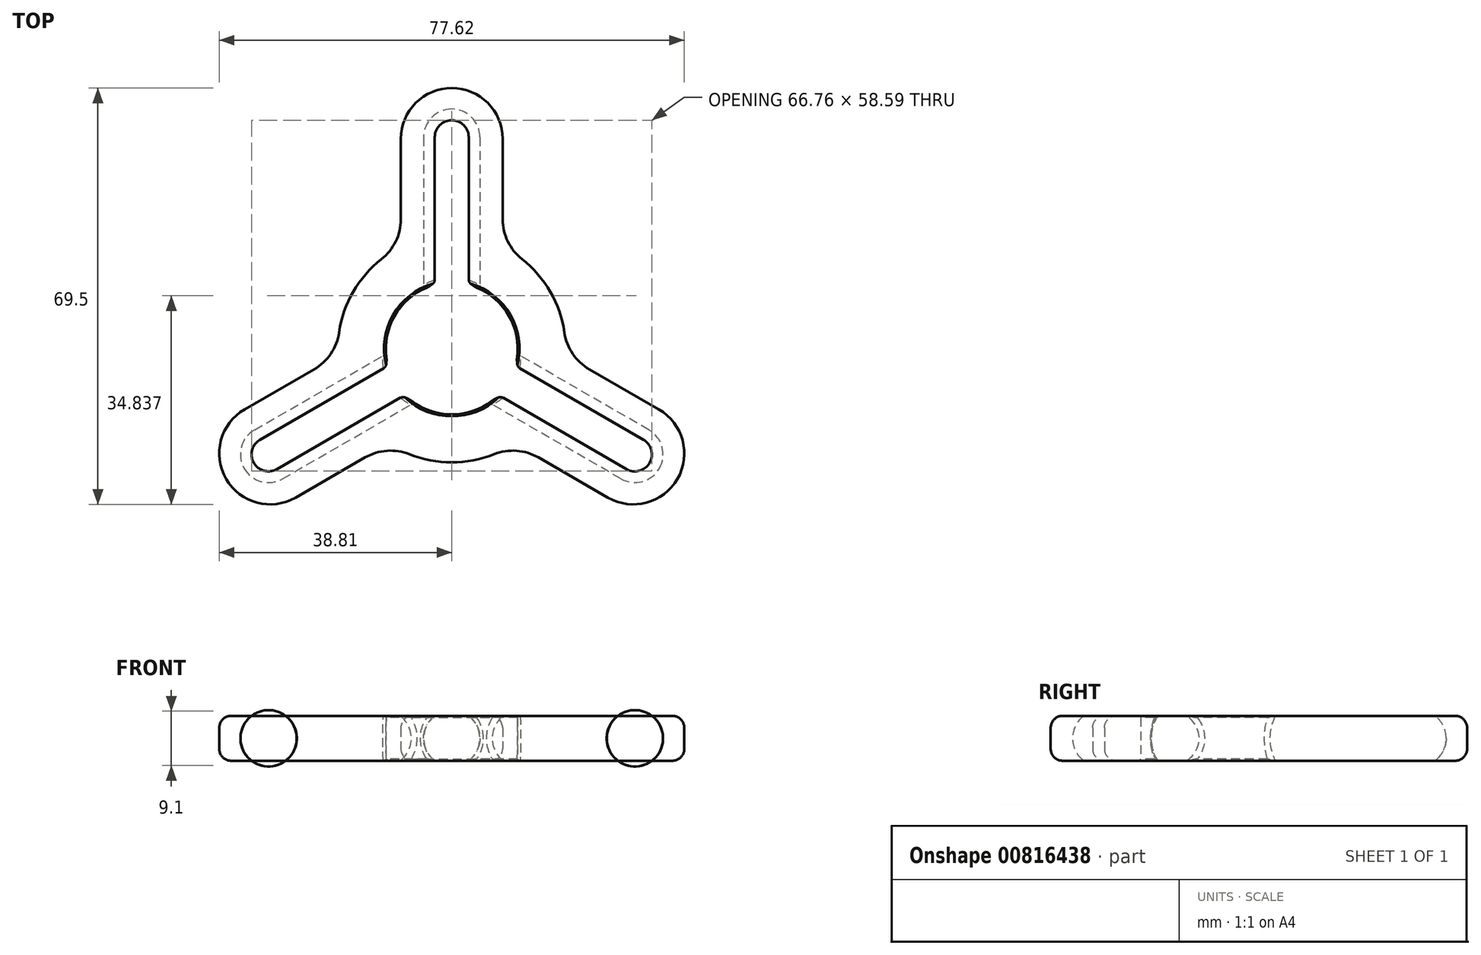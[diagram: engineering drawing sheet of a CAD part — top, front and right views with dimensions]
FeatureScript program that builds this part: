
annotation { "Feature Type Name" : "Feature", "Feature Type Description" : "" }
export const myFeature = defineFeature(function(context is Context, id is Id, definition is map)
    precondition{}
    {
        {
            var Q0;
            Q0=qCreatedBy(makeId("Top.planeOp"),FACE);
            var sketch = newSketch(context, id + "F0", { "sketchPlane" : qUnion([Q0])});
            skLineSegment(sketch, "E0", {"start": v(-9.53, 5.5) * mm, "end": v(0, 0) * mm, "construction": true});
            skLineSegment(sketch, "E1", {"start": v(0, 0) * mm, "end": v(9.53, 5.5) * mm, "construction": true});
            skArc(sketch, "E2", {"start": v(9.53, 5.5) * mm, "mid": v(0, 11) * mm, "end": v(-9.53, 5.5) * mm});
            skLineSegment(sketch, "E3", {"start": v(0, 0) * mm, "end": v(0, 11) * mm, "construction": true});
            skLineSegment(sketch, "E4", {"start": v(-9.53, 5.5) * mm, "end": v(-16.45, 9.5) * mm});
            skLineSegment(sketch, "E5", {"start": v(9.53, 5.5) * mm, "end": v(21.03, 12.14) * mm});
            skLineSegment(sketch, "E6", {"start": v(-8.5, 17) * mm, "end": v(-8.5, 35) * mm});
            skLineSegment(sketch, "E7", {"start": v(8.5, 35) * mm, "end": v(8.5, 17) * mm});
            skArc(sketch, "E8", {"start": v(-16.45, 9.5) * mm, "mid": v(-13.03, 13.83) * mm, "end": v(-8.5, 17) * mm});
            skArc(sketch, "E9", {"start": v(-8.5, 35) * mm, "mid": v(0, 43.5) * mm, "end": v(8.5, 35) * mm});
            skArc(sketch, "E10.trimOffspring", {"start": v(8.5, 17) * mm, "mid": v(13.03, 13.83) * mm, "end": v(16.45, 9.5) * mm});
            skSolve(sketch);
        }
        {
            var Q0;
            Q0=qSketchRegion(id+"F0",true);
            extrude(context, id + "F1", {"entities" : qUnion([Q0]), "depth" : 3.75 * mm, "offsetDistance" : 25 * mm, "hasSecondDirection" : true, "secondDirectionOppositeDirection" : true, "secondDirectionDepth" : 3.75 * mm});
        }
        {
            var Q0;
            Q0=qCreatedBy(makeId("Front.planeOp"),FACE);
            var sketch = newSketch(context, id + "F2", { "sketchPlane" : qUnion([Q0])});
            skCircle(sketch, "E11", {"center": v(0, 0) * mm, "radius": 4.7 * mm});
            skSolve(sketch);
        }
        {
            var Q0;
            Q0=qSketchRegion(id+"F2",true);
            extrude(context, id + "F3", {"entities" : qUnion([Q0]), "oppositeDirection" : true, "depth" : 40 * mm, "offsetDistance" : 25 * mm});
        }
        {
            var Q0;
            Q0=makeQuery(id+"F3.opExtrude","CAP_EDGE",EDGE,{"disambiguationData":[OSD([sQuery(id+"F2.wireOp",EDGE,"E11")])],"isStart":false});
            fillet(context, id + "F4", {"entities" : qUnion([Q0]), "radius" : 4.7 * mm, "tangentPropagation" : true, "allowEdgeOverflow" : false});
        }
        {
            var Q0;
            Q0=makeQuery(id+"F1.opExtrude","SWEPT_EDGE",EDGE,{"disambiguationData":[OSD([sQuery(id+"F0.wireOp",EDGE,"E6"),sQuery(id+"F0.wireOp",EDGE,"E8")])]});
            var Q1;
            Q1=makeQuery(id+"F1.opExtrude","SWEPT_EDGE",EDGE,{"disambiguationData":[OSD([sQuery(id+"F0.wireOp",EDGE,"E7"),sQuery(id+"F0.wireOp",EDGE,"E10.trimOffspring")])]});
            fillet(context, id + "F5", {"entities" : qUnion([Q0, Q1]), "radius" : 8.5 * mm, "tangentPropagation" : true, "allowEdgeOverflow" : false});
        }
        {
            var Q0;
            Q0=makeQuery(id+"F3.opExtrude","SWEPT_BODY",BODY,{"disambiguationData":[OSD([sQuery(id+"F2.wireOp",EDGE,"E11")])]});
            var Q1;
            Q1=makeQuery(id+"F1.opExtrude","SWEPT_BODY",BODY,{"disambiguationData":[OSD([sQuery(id+"F0.wireOp",EDGE,"E2"),sQuery(id+"F0.wireOp",EDGE,"E4"),sQuery(id+"F0.wireOp",EDGE,"E5"),sQuery(id+"F0.wireOp",EDGE,"E6"),sQuery(id+"F0.wireOp",EDGE,"E7"),sQuery(id+"F0.wireOp",EDGE,"E8"),sQuery(id+"F0.wireOp",EDGE,"E9"),sQuery(id+"F0.wireOp",EDGE,"E10.trimOffspring")])]});
            booleanBodies(context, id + "F6", {"operationType" : BooleanOperationType.SUBTRACTION, "tools" : qUnion([Q0]), "targets" : qUnion([Q1])});
        }
        {
            var Q0;
            {var subQ0=sQuery(id+"F0.wireOp",EDGE,"E2");var subQ1=sQuery(id+"F0.wireOp",EDGE,"E4");Q0=makeQuery(id+"F6.opBoolean","SPLIT",EDGE,{"disambiguationData":[TD([makeQuery(id+"F1.opExtrude","SWEPT_FACE",FACE,{"disambiguationData":[OSD([subQ1])]})])],"derivedFrom":makeQuery(id+"F1.opExtrude","CAP_EDGE",EDGE,{"disambiguationData":[OSD([subQ0])],"isStart":false})});}
            var Q1;
            {var subQ0=sQuery(id+"F0.wireOp",EDGE,"E2");var subQ1=sQuery(id+"F0.wireOp",EDGE,"E4");Q1=makeQuery(id+"F6.opBoolean","SPLIT",EDGE,{"disambiguationData":[TD([makeQuery(id+"F1.opExtrude","SWEPT_FACE",FACE,{"disambiguationData":[OSD([subQ1])]})])],"derivedFrom":makeQuery(id+"F1.opExtrude","CAP_EDGE",EDGE,{"disambiguationData":[OSD([subQ0])],"isStart":true})});}
            var Q2;
            {var subQ0=sQuery(id+"F0.wireOp",EDGE,"E2");var subQ1=sQuery(id+"F0.wireOp",EDGE,"E5");Q2=makeQuery(id+"F6.opBoolean","SPLIT",EDGE,{"disambiguationData":[TD([makeQuery(id+"F1.opExtrude","SWEPT_FACE",FACE,{"disambiguationData":[OSD([subQ1])]})])],"derivedFrom":makeQuery(id+"F1.opExtrude","CAP_EDGE",EDGE,{"disambiguationData":[OSD([subQ0])],"isStart":true})});}
            var Q3;
            {var subQ0=sQuery(id+"F0.wireOp",EDGE,"E2");var subQ1=sQuery(id+"F0.wireOp",EDGE,"E5");Q3=makeQuery(id+"F6.opBoolean","SPLIT",EDGE,{"disambiguationData":[TD([makeQuery(id+"F1.opExtrude","SWEPT_FACE",FACE,{"disambiguationData":[OSD([subQ1])]})])],"derivedFrom":makeQuery(id+"F1.opExtrude","CAP_EDGE",EDGE,{"disambiguationData":[OSD([subQ0])],"isStart":false})});}
            chamfer(context, id + "F7", {"entities" : qUnion([Q0, Q1, Q2, Q3]), "width" : 0.3 * mm, "tangentPropagation" : true});
        }
        {
            var Q0;
            Q0=makeQuery(id+"F6.opBoolean","INTERSECT",EDGE,{"disambiguationData":[OD(1.0)],"derivedFrom":[makeQuery(id+"F1.opExtrude","SWEPT_FACE",FACE,{"disambiguationData":[OSD([sQuery(id+"F0.wireOp",EDGE,"E2")])]}),makeQuery(id+"F3.opExtrude","SWEPT_FACE",FACE,{"disambiguationData":[OSD([sQuery(id+"F2.wireOp",EDGE,"E11")])]})]});
            var Q1;
            Q1=makeQuery(id+"F6.opBoolean","INTERSECT",EDGE,{"disambiguationData":[OD(0.0)],"derivedFrom":[makeQuery(id+"F1.opExtrude","SWEPT_FACE",FACE,{"disambiguationData":[OSD([sQuery(id+"F0.wireOp",EDGE,"E2")])]}),makeQuery(id+"F3.opExtrude","SWEPT_FACE",FACE,{"disambiguationData":[OSD([sQuery(id+"F2.wireOp",EDGE,"E11")])]})]});
            fillet(context, id + "F8", {"entities" : qUnion([Q0, Q1]), "radius" : 1 * mm, "tangentPropagation" : true, "allowEdgeOverflow" : false});
        }
        {
            var Q0;
            Q0=qCreatedBy(makeId("Front.planeOp"),FACE);
            var sketch = newSketch(context, id + "F9", { "sketchPlane" : qUnion([Q0])});
            skLineSegment(sketch, "E12", {"start": v(0, 0) * mm, "end": v(0, 24.93) * mm});
            skSolve(sketch);
        }
        {
            var Q0;
            Q0=makeQuery(id+"F1.opExtrude","SWEPT_BODY",BODY,{"disambiguationData":[OSD([sQuery(id+"F0.wireOp",EDGE,"E2"),sQuery(id+"F0.wireOp",EDGE,"E4"),sQuery(id+"F0.wireOp",EDGE,"E5"),sQuery(id+"F0.wireOp",EDGE,"E6"),sQuery(id+"F0.wireOp",EDGE,"E7"),sQuery(id+"F0.wireOp",EDGE,"E8"),sQuery(id+"F0.wireOp",EDGE,"E9"),sQuery(id+"F0.wireOp",EDGE,"E10.trimOffspring")])]});
            var Q1;
            Q1=sQuery(id+"F9.wireOp",EDGE,"E12");
            circularPattern(context, id + "F10", {"operationType" : NewBodyOperationType.ADD, "entities" : qUnion([Q0]), "axis" : qUnion([Q1]), "angle" : 360 * degree, "instanceCount" : 3, "equalSpace" : true});
        }
        {
            var Q0;
            Q0=makeQuery(id+"F1.opExtrude","CAP_EDGE",EDGE,{"disambiguationData":[OSD([sQuery(id+"F0.wireOp",EDGE,"E6")])],"isStart":false});
            var Q1;
            Q1=makeQuery(id+"F10.opPattern","COPY",EDGE,{"derivedFrom":makeQuery(id+"F1.opExtrude","CAP_EDGE",EDGE,{"disambiguationData":[OSD([sQuery(id+"F0.wireOp",EDGE,"E6")])],"isStart":true}),"instanceName":"1"});
            fillet(context, id + "F11", {"entities" : qUnion([Q0, Q1]), "radius" : 2 * mm, "tangentPropagation" : true, "allowEdgeOverflow" : false});
        }
    });
